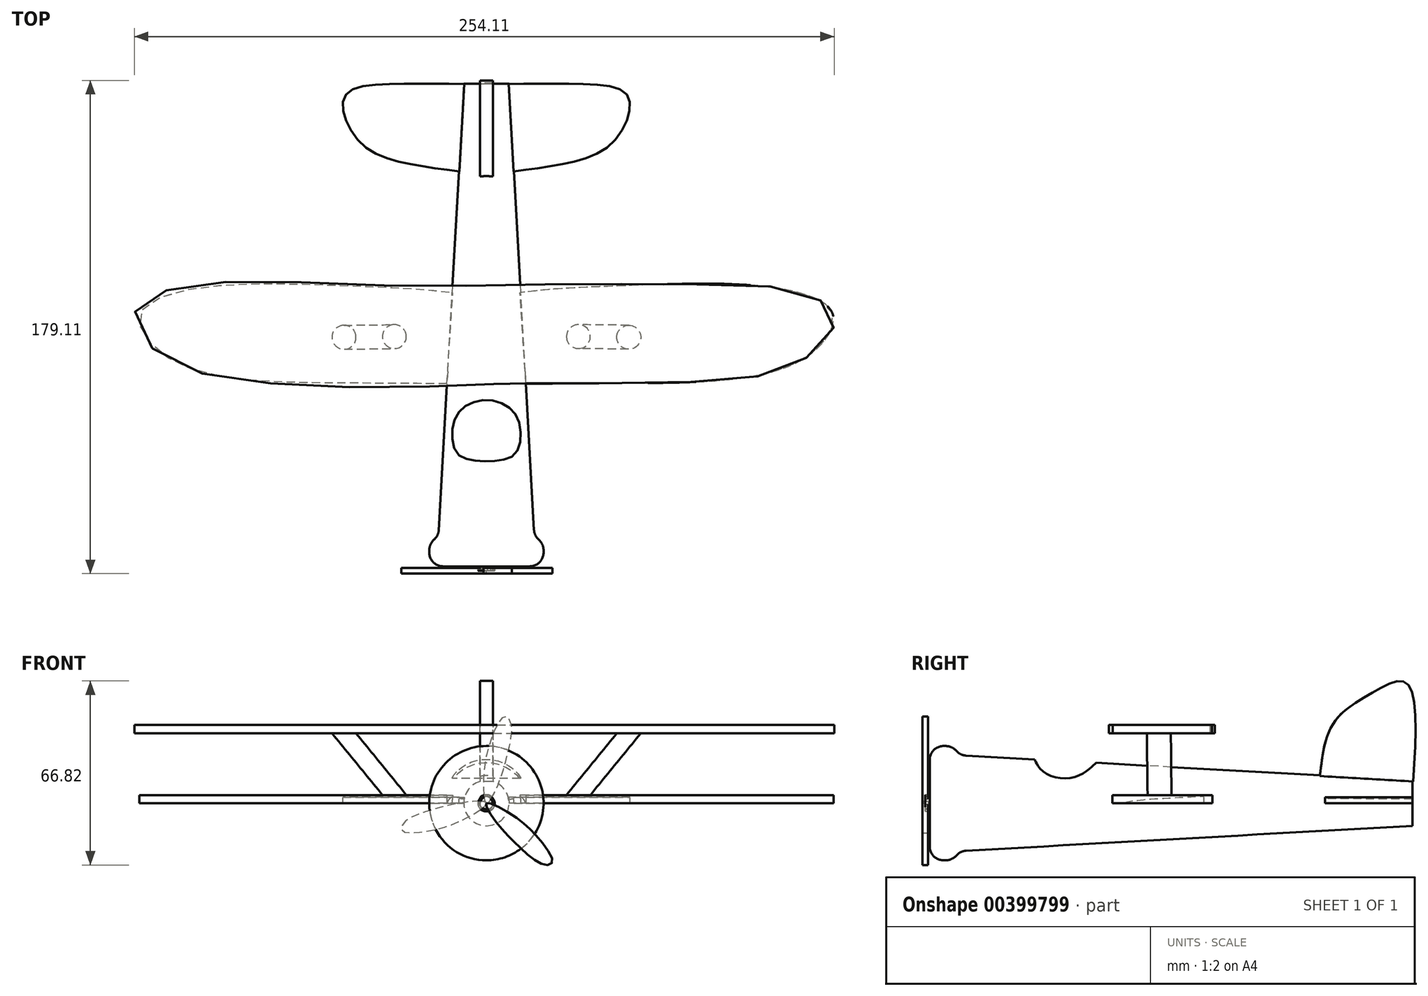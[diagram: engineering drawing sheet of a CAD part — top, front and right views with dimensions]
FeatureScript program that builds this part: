
annotation { "Feature Type Name" : "Feature", "Feature Type Description" : "" }
export const myFeature = defineFeature(function(context is Context, id is Id, definition is map)
    precondition{}
    {
        {
            var Q0;
            Q0=qCreatedBy(makeId("Front.planeOp"),FACE);
            cPlane(context, id + "F0", {"entities" : qUnion([Q0]), "cplaneType" : CPlaneType.OFFSET, "offset" : 164.72 * mm, "oppositeDirection" : true, "width" : 152.4 * mm, "height" : 152.4 * mm});
        }
        {
            var Q0;
            Q0=qCreatedBy(id+"F0.planeOp",FACE);
            var sketch = newSketch(context, id + "F1", { "sketchPlane" : qUnion([Q0])});
            skCircle(sketch, "E0", {"center": v(0, 0) * mm, "radius": 8.22 * mm});
            skSolve(sketch);
        }
        {
            var Q0;
            Q0=qCreatedBy(makeId("Front.planeOp"),FACE);
            var sketch = newSketch(context, id + "F2", { "sketchPlane" : qUnion([Q0])});
            skCircle(sketch, "E1", {"center": v(0, 0) * mm, "radius": 17.44 * mm});
            skSolve(sketch);
        }
        {
            var Q0;
            Q0 = qSketchRegion(id + "F2", true);
            var Q1;
            Q1 = qSketchRegion(id + "F1", true);
            loft(context, id + "F3", {"sheetProfilesArray" : [{ "sheetProfileEntities" : qUnion([Q0]) }, { "sheetProfileEntities" : qUnion([Q1]) }]});
        }
        {
            var Q0;
            Q0=qCreatedBy(makeId("Right.planeOp"),FACE);
            var sketch = newSketch(context, id + "F4", { "sketchPlane" : qUnion([Q0])});
            skFitSpline(sketch, "E2", {"points": [v(131.04, 9.25) * mm, v(135.83, 28.79) * mm, v(149.44, 39.75) * mm, v(162.3, 43.78) * mm, v(164.94, 7.86) * mm], "startDerivative": vector(9.62, 88.43) * mm, "endDerivative": vector(-9.78, -150.4) * mm});
            skLineSegment(sketch, "E3", {"start": v(131.04, 9.25) * mm, "end": v(164.94, 7.86) * mm});
            skSolve(sketch);
        }
        {
            var Q0;
            Q0=makeQuery(id+"F4.imprint","IMPRINT",FACE,{"disambiguationData":[TD([[makeQuery(id+"F4.imprint","IMPRINT",EDGE,{"derivedFrom":sQuery(id+"F4.wireOp",EDGE,"E2")}),-1.0]])]});
            extrude(context, id + "F5", {"entities" : qUnion([Q0]), "operationType" : NewBodyOperationType.ADD, "depth" : 2.34 * mm, "hasSecondDirection" : true, "secondDirectionOppositeDirection" : true, "secondDirectionDepth" : 2.34 * mm});
        }
        {
            var Q0;
            Q0=qCreatedBy(makeId("Top.planeOp"),FACE);
            var sketch = newSketch(context, id + "F6", { "sketchPlane" : qUnion([Q0])});
            skFitSpline(sketch, "E4", {"points": [v(9.86, 132.89) * mm, v(27.6, 135.5) * mm, v(43.58, 141.4) * mm, v(51.62, 153.35) * mm, v(50.44, 161.4) * mm, v(34.7, 164.6) * mm, v(8.1, 164.6) * mm], "startDerivative": vector(101.17, 12.6) * mm, "endDerivative": vector(-126.94, -1.65) * mm});
            skLineSegment(sketch, "E5", {"start": v(9.86, 132.89) * mm, "end": v(8.1, 164.6) * mm});
            skSolve(sketch);
        }
        {
            var Q0;
            Q0 = qSketchRegion(id + "F6", true);
            extrude(context, id + "F7", {"entities" : qUnion([Q0]), "operationType" : NewBodyOperationType.ADD, "depth" : 2.08 * mm});
        }
        {
            var Q0;
            Q0=makeQuery(id+"F3.opLoft","SWEPT_BODY",BODY,{"disambiguationData":[OSD([makeQuery(id+"F1.imprint","IMPRINT",FACE,{"disambiguationData":[TD([[makeQuery(id+"F1.imprint","IMPRINT",EDGE,{"derivedFrom":sQuery(id+"F1.wireOp",EDGE,"E0")}),1.0]])]}),makeQuery(id+"F2.imprint","IMPRINT",FACE,{"disambiguationData":[TD([[makeQuery(id+"F2.imprint","IMPRINT",EDGE,{"derivedFrom":sQuery(id+"F2.wireOp",EDGE,"E1")}),1.0]])]})])]});
            var Q1;
            Q1=qCreatedBy(makeId("Right.planeOp"),FACE);
            mirror(context, id + "F8", {"operationType" : NewBodyOperationType.ADD, "entities" : qUnion([Q0]), "mirrorPlane" : qUnion([Q1])});
        }
        {
            var Q0;
            Q0=qCreatedBy(makeId("Top.planeOp"),FACE);
            var sketch = newSketch(context, id + "F9", { "sketchPlane" : qUnion([Q0])});
            skFitSpline(sketch, "E6", {"points": [v(14.36, 55.74) * mm, v(51.6, 55.97) * mm, v(96.82, 58.47) * mm, v(120.14, 68.59) * mm, v(125.73, 81.08) * mm, v(104.67, 90.6) * mm, v(52.8, 91.43) * mm, v(26.26, 90.24) * mm, v(12.22, 88.81) * mm], "startDerivative": vector(247.48, 1.86) * mm, "endDerivative": vector(-150.68, -17.79) * mm});
            skLineSegment(sketch, "E7", {"start": v(14.36, 55.74) * mm, "end": v(12.22, 88.81) * mm});
            skSolve(sketch);
        }
        {
            var Q0;
            Q0=makeQuery(id+"F9.imprint","IMPRINT",FACE,{"disambiguationData":[TD([[makeQuery(id+"F9.imprint","IMPRINT",EDGE,{"derivedFrom":sQuery(id+"F9.wireOp",EDGE,"E6")}),1.0]])]});
            extrude(context, id + "F10", {"entities" : qUnion([Q0]), "operationType" : NewBodyOperationType.ADD, "depth" : 2.96 * mm});
        }
        {
            var Q0;
            Q0=makeQuery(id+"F3.opLoft","SWEPT_BODY",BODY,{"disambiguationData":[OSD([makeQuery(id+"F1.imprint","IMPRINT",FACE,{"disambiguationData":[TD([[makeQuery(id+"F1.imprint","IMPRINT",EDGE,{"derivedFrom":sQuery(id+"F1.wireOp",EDGE,"E0")}),1.0]])]}),makeQuery(id+"F2.imprint","IMPRINT",FACE,{"disambiguationData":[TD([[makeQuery(id+"F2.imprint","IMPRINT",EDGE,{"derivedFrom":sQuery(id+"F2.wireOp",EDGE,"E1")}),1.0]])]})])]});
            var Q1;
            Q1=qCreatedBy(makeId("Right.planeOp"),FACE);
            mirror(context, id + "F11", {"operationType" : NewBodyOperationType.ADD, "entities" : qUnion([Q0]), "mirrorPlane" : qUnion([Q1])});
        }
        {
            var Q0;
            Q0=qCreatedBy(makeId("Front.planeOp"),FACE);
            var sketch = newSketch(context, id + "F12", { "sketchPlane" : qUnion([Q0])});
            skCircle(sketch, "E8", {"center": v(0, 0) * mm, "radius": 20.76 * mm});
            skSolve(sketch);
        }
        {
            var Q0;
            Q0=makeQuery(id+"F12.imprint","IMPRINT",FACE,{"disambiguationData":[TD([[makeQuery(id+"F12.imprint","IMPRINT",EDGE,{"derivedFrom":sQuery(id+"F12.wireOp",EDGE,"E8")}),1.0]])]});
            extrude(context, id + "F13", {"entities" : qUnion([Q0]), "operationType" : NewBodyOperationType.ADD, "depth" : 10.62 * mm});
        }
        {
            var Q0;
            Q0=makeQuery(id+"F13.opExtrude","CAP_EDGE",EDGE,{"disambiguationData":[OSD([sQuery(id+"F12.wireOp",EDGE,"E8")])],"isStart":false});
            fillet(context, id + "F14", {"entities" : qUnion([Q0]), "radius" : 5.08 * mm, "tangentPropagation" : true, "allowEdgeOverflow" : false});
        }
        {
            var Q0;
            Q0=makeQuery(id+"F13.opExtrude","CAP_EDGE",EDGE,{"disambiguationData":[OSD([sQuery(id+"F12.wireOp",EDGE,"E8")])],"isStart":true});
            fillet(context, id + "F15", {"entities" : qUnion([Q0]), "radius" : 5.08 * mm, "tangentPropagation" : true, "allowEdgeOverflow" : false});
        }
        {
            var Q0;
            Q0=makeQuery(id+"F15.opFillet","BLEND_EDGE",EDGE,{"blendedFrom":[makeQuery(id+"F13.opExtrude","CAP_EDGE",EDGE,{"disambiguationData":[OSD([sQuery(id+"F12.wireOp",EDGE,"E8")])],"isStart":true}),makeQuery(id+"F3.opLoft","SWEPT_FACE",FACE,{"disambiguationData":[OSD([sQuery(id+"F1.wireOp",EDGE,"E0"),sQuery(id+"F2.wireOp",EDGE,"E1")])]})],"blendedInto":[makeQuery(id+"F3.opLoft","SWEPT_FACE",FACE,{"disambiguationData":[OSD([sQuery(id+"F1.wireOp",EDGE,"E0"),sQuery(id+"F2.wireOp",EDGE,"E1")])]})]});
            fillet(context, id + "F16", {"entities" : qUnion([Q0]), "radius" : 5.08 * mm, "tangentPropagation" : true, "allowEdgeOverflow" : false});
        }
        {
            var Q0;
            Q0=qCreatedBy(makeId("Right.planeOp"),FACE);
            var sketch = newSketch(context, id + "F17", { "sketchPlane" : qUnion([Q0])});
            skLineSegment(sketch, "E9.bottom", {"start": v(-10.62, 3.08) * mm, "end": v(-12.25, 3.08) * mm});
            skLineSegment(sketch, "E9.top", {"start": v(-10.62, -2.18) * mm, "end": v(-12.25, -2.18) * mm});
            skLineSegment(sketch, "E9.left", {"start": v(-10.62, 3.08) * mm, "end": v(-10.62, -2.18) * mm});
            skLineSegment(sketch, "E9.right", {"start": v(-12.25, 3.08) * mm, "end": v(-12.25, -2.18) * mm});
            skSolve(sketch);
        }
        {
            var Q0;
            Q0=makeQuery(id+"F17.imprint","IMPRINT",FACE,{"disambiguationData":[TD([[makeQuery(id+"F17.imprint","IMPRINT",EDGE,{"derivedFrom":sQuery(id+"F17.wireOp",EDGE,"E9.bottom")}),1.0]])]});
            extrude(context, id + "F18", {"entities" : qUnion([Q0]), "depth" : 2.67 * mm, "hasSecondDirection" : true, "secondDirectionOppositeDirection" : true, "secondDirectionDepth" : 2.67 * mm});
        }
        {
            var Q0;
            Q0=qCreatedBy(makeId("Front.planeOp"),FACE);
            cPlane(context, id + "F19", {"entities" : qUnion([Q0]), "cplaneType" : CPlaneType.OFFSET, "offset" : 11.22 * mm, "width" : 152.4 * mm, "height" : 152.4 * mm});
        }
        {
            var Q0;
            Q0=makeQuery(id+"F18.opExtrude","CAP_EDGE",EDGE,{"disambiguationData":[OSD([sQuery(id+"F17.wireOp",EDGE,"E9.bottom")])],"isStart":true});
            var Q1;
            Q1=makeQuery(id+"F18.opExtrude","CAP_EDGE",EDGE,{"disambiguationData":[OSD([sQuery(id+"F17.wireOp",EDGE,"E9.bottom")])],"isStart":false});
            var Q2;
            Q2=makeQuery(id+"F18.opExtrude","CAP_EDGE",EDGE,{"disambiguationData":[OSD([sQuery(id+"F17.wireOp",EDGE,"E9.top")])],"isStart":true});
            var Q3;
            Q3=makeQuery(id+"F18.opExtrude","CAP_EDGE",EDGE,{"disambiguationData":[OSD([sQuery(id+"F17.wireOp",EDGE,"E9.top")])],"isStart":false});
            fillet(context, id + "F20", {"entities" : qUnion([Q0, Q1, Q2, Q3]), "radius" : 2.54 * mm, "tangentPropagation" : true, "allowEdgeOverflow" : false});
        }
        {
            var Q0;
            Q0=qCreatedBy(id+"F19.planeOp",FACE);
            var sketch = newSketch(context, id + "F21", { "sketchPlane" : qUnion([Q0])});
            skFitSpline(sketch, "E10", {"points": [v(0, 0) * mm, v(3.5, -6.75) * mm, v(11.7, -15.66) * mm, v(20.73, -22.28) * mm, v(23.95, -21.35) * mm, v(18.5, -12.26) * mm, v(9.36, -4.3) * mm, v(0, 0) * mm]});
            skSolve(sketch);
        }
        {
            var Q0;
            Q0=makeQuery(id+"F21.imprint","IMPRINT",FACE,{"disambiguationData":[TD([[makeQuery(id+"F21.imprint","IMPRINT",EDGE,{"derivedFrom":sQuery(id+"F21.wireOp",EDGE,"E10")}),1.0]])]});
            extrude(context, id + "F22", {"entities" : qUnion([Q0]), "operationType" : NewBodyOperationType.ADD, "depth" : 2.05 * mm});
        }
        {
            var Q0;
            Q0=qCreatedBy(makeId("Right.planeOp"),FACE);
            var sketch = newSketch(context, id + "F23", { "sketchPlane" : qUnion([Q0])});
            skLineSegment(sketch, "E11", {"start": v(-76.66, 0) * mm, "end": v(164, 0) * mm});
            skSolve(sketch);
        }
        {
            var Q0;
            Q0=makeQuery(id+"F18.opExtrude","SWEPT_BODY",BODY,{"disambiguationData":[OSD([sQuery(id+"F17.wireOp",EDGE,"E9.bottom"),sQuery(id+"F17.wireOp",EDGE,"E9.top"),sQuery(id+"F17.wireOp",EDGE,"E9.left"),sQuery(id+"F17.wireOp",EDGE,"E9.right")])]});
            var Q1;
            Q1=sQuery(id+"F23.wireOp",EDGE,"E11");
            circularPattern(context, id + "F24", {"entities" : qUnion([Q0]), "axis" : qUnion([Q1]), "angle" : 360 * degree, "instanceCount" : 3, "equalSpace" : true});
        }
        {
            var Q0;
            Q0=qCreatedBy(makeId("Top.planeOp"),FACE);
            var sketch = newSketch(context, id + "F25", { "sketchPlane" : qUnion([Q0])});
            skCircle(sketch, "E12", {"center": v(107.78, 76.07) * mm, "radius": 6.58 * mm});
            skSolve(sketch);
        }
        {
            var Q0;
            Q0=sQuery(id+"F25.wireOp",EDGE,"E12");
            extrude(context, id + "F26", {"bodyType" : ToolBodyType.SURFACE, "surfaceEntities" : qUnion([Q0]), "depth" : 25.4 * mm});
        }
        {
            var Q0;
            Q0=makeQuery(id+"F26.opExtrude","SWEPT_BODY",BODY,{"disambiguationData":[OSD([sQuery(id+"F25.wireOp",EDGE,"E12")])]});
            var Q1;
            Q1=qCreatedBy(makeId("Right.planeOp"),FACE);
            mirror(context, id + "F27", {"entities" : qUnion([Q0]), "mirrorPlane" : qUnion([Q1])});
        }
        {
            var Q0;
            Q0=qCreatedBy(makeId("Top.planeOp"),FACE);
            cPlane(context, id + "F28", {"entities" : qUnion([Q0]), "cplaneType" : CPlaneType.OFFSET, "offset" : 25.4 * mm, "width" : 152.4 * mm, "height" : 152.4 * mm});
        }
        {
            var Q0;
            Q0=qCreatedBy(id+"F28.planeOp",FACE);
            var sketch = newSketch(context, id + "F29", { "sketchPlane" : qUnion([Q0])});
            skFitSpline(sketch, "E13", {"points": [v(14.55, 55.84) * mm, v(75.23, 56.37) * mm, v(108.57, 61.3) * mm, v(124.6, 72.75) * mm, v(125.75, 80.82) * mm, v(116.15, 88.62) * mm, v(75.71, 91.82) * mm, v(24, 91.82) * mm, v(-33.71, 91.3) * mm, v(-91.14, 92.8) * mm, v(-121, 87.91) * mm, v(-127.8, 80.4) * mm, v(-118.02, 65.92) * mm, v(-85.38, 56.5) * mm, v(-29.35, 54.57) * mm, v(6.25, 55.8) * mm, v(14.55, 55.84) * mm]});
            skSolve(sketch);
        }
        {
            var Q0;
            Q0=makeQuery(id+"F29.imprint","IMPRINT",FACE,{"disambiguationData":[TD([[makeQuery(id+"F29.imprint","IMPRINT",EDGE,{"derivedFrom":sQuery(id+"F29.wireOp",EDGE,"E13")}),1.0]])]});
            extrude(context, id + "F30", {"entities" : qUnion([Q0]), "depth" : 2.97 * mm});
        }
        {
            var Q0;
            Q0=qCreatedBy(makeId("Right.planeOp"),FACE);
            var sketch = newSketch(context, id + "F31", { "sketchPlane" : qUnion([Q0])});
            skFitSpline(sketch, "E14", {"points": [v(27.12, 17.03) * mm, v(30.65, 11.42) * mm, v(41.24, 9.25) * mm, v(51.1, 15.86) * mm], "startDerivative": vector(8.51, -22.24) * mm, "endDerivative": vector(24.41, 23.36) * mm});
            skLineSegment(sketch, "E15", {"start": v(51.1, 15.86) * mm, "end": v(27.12, 17.03) * mm});
            skSolve(sketch);
        }
        {
            var Q0;
            Q0 = qSketchRegion(id + "F31", true);
            extrude(context, id + "F32", {"entities" : qUnion([Q0]), "operationType" : NewBodyOperationType.REMOVE, "endBound" : BoundingType.THROUGH_ALL, "oppositeDirection" : true, "depth" : 25.4 * mm, "hasSecondDirection" : true, "secondDirectionOppositeDirection" : false, "secondDirectionDepth" : 37.34 * mm});
        }
        {
            var Q0;
            Q0=makeQuery(id+"F11.opPattern","COPY",FACE,{"derivedFrom":makeQuery(id+"F10.opExtrude","CAP_FACE",FACE,{"disambiguationData":[OSD([sQuery(id+"F9.wireOp",EDGE,"E6"),sQuery(id+"F9.wireOp",EDGE,"E7")])],"isStart":false}),"instanceName":"1"});
            var sketch = newSketch(context, id + "F33", { "sketchPlane" : qUnion([Q0])});
            skCircle(sketch, "E16", {"center": v(-33.41, 72.86) * mm, "radius": 4.34 * mm});
            skSolve(sketch);
        }
        {
            var Q0;
            Q0=makeQuery(id+"F30.opExtrude","CAP_FACE",FACE,{"disambiguationData":[OSD([sQuery(id+"F29.wireOp",EDGE,"E13")])],"isStart":true});
            var sketch = newSketch(context, id + "F34", { "sketchPlane" : qUnion([Q0])});
            skCircle(sketch, "E17", {"center": v(-51.7, -72.62) * mm, "radius": 4.36 * mm});
            skSolve(sketch);
        }
        {
            var Q0;
            Q0 = qSketchRegion(id + "F33", true);
            var Q1;
            Q1 = qSketchRegion(id + "F34", true);
            loft(context, id + "F35", {"sheetProfilesArray" : [{ "sheetProfileEntities" : qUnion([Q0]) }, { "sheetProfileEntities" : qUnion([Q1]) }]});
        }
        {
            var Q0;
            Q0=makeQuery(id+"F35.opLoft","SWEPT_BODY",BODY,{"disambiguationData":[OSD([makeQuery(id+"F33.imprint","IMPRINT",FACE,{"disambiguationData":[TD([[makeQuery(id+"F33.imprint","IMPRINT",EDGE,{"derivedFrom":sQuery(id+"F33.wireOp",EDGE,"E16")}),1.0]])]}),makeQuery(id+"F34.imprint","IMPRINT",FACE,{"disambiguationData":[TD([[makeQuery(id+"F34.imprint","IMPRINT",EDGE,{"derivedFrom":sQuery(id+"F34.wireOp",EDGE,"E17")}),1.0]])]})])]});
            var Q1;
            Q1=qCreatedBy(makeId("Right.planeOp"),FACE);
            mirror(context, id + "F36", {"entities" : qUnion([Q0]), "mirrorPlane" : qUnion([Q1])});
        }
    });
